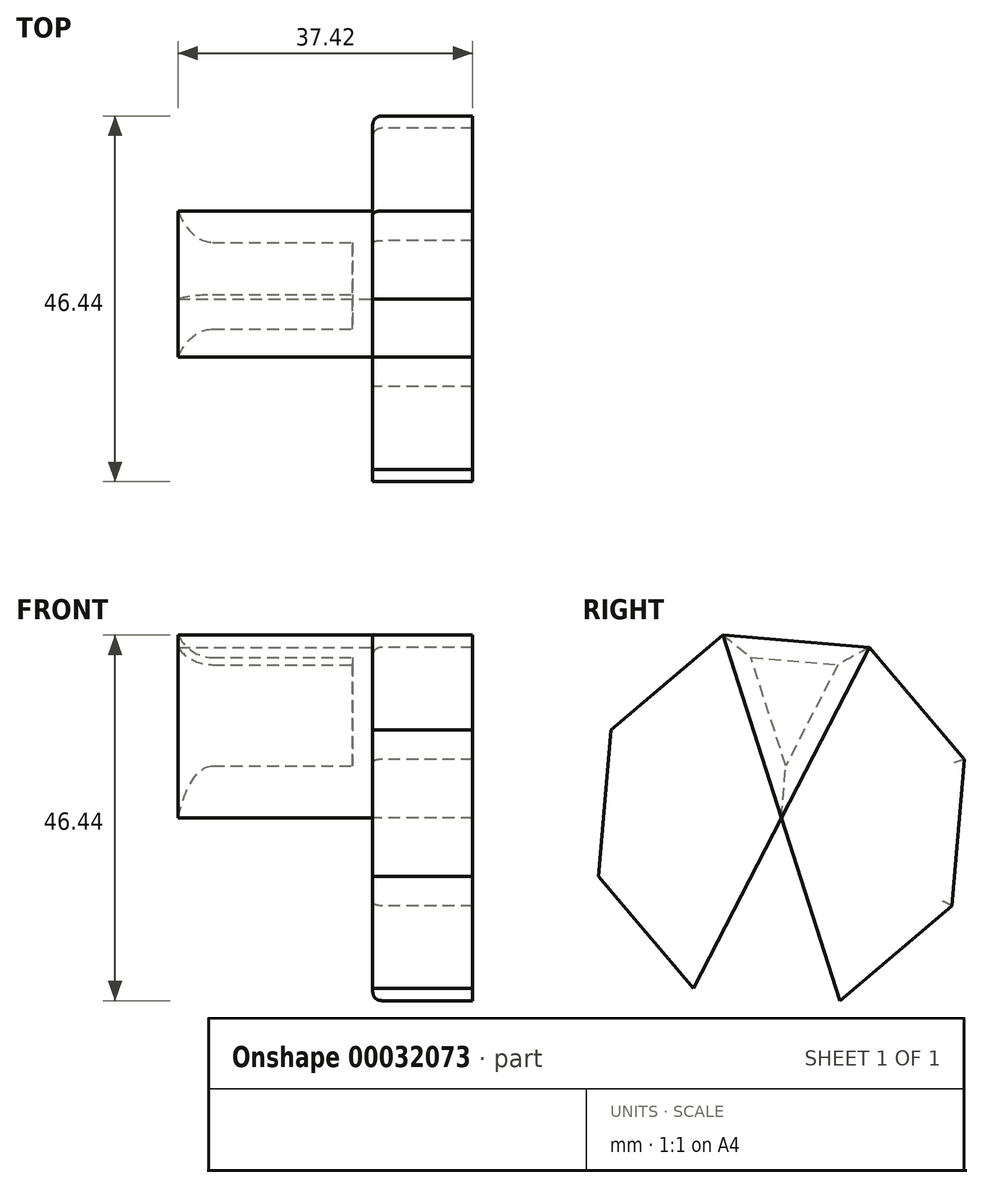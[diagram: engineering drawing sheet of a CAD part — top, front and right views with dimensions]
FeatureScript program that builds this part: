
annotation { "Feature Type Name" : "Feature", "Feature Type Description" : "" }
export const myFeature = defineFeature(function(context is Context, id is Id, definition is map)
    precondition{}
    {
        {
            var Q0;
            Q0=qCreatedBy(makeId("Right.planeOp"),FACE);
            var sketch = newSketch(context, id + "F0", { "sketchPlane" : qUnion([Q0])});
            skCircle(sketch, "E0.cCircle", {"center": v(0, 0) * mm, "radius": 24.38 * mm, "construction": true});
            skLineSegment(sketch, "E0.0", {"start": v(-21.67, 11.17) * mm, "end": v(-7.42, 23.22) * mm});
            skLineSegment(sketch, "E0.1", {"start": v(-7.42, 23.22) * mm, "end": v(11.17, 21.67) * mm});
            skLineSegment(sketch, "E0.2", {"start": v(11.17, 21.67) * mm, "end": v(23.22, 7.42) * mm});
            skLineSegment(sketch, "E0.3", {"start": v(23.22, 7.42) * mm, "end": v(21.67, -11.17) * mm});
            skLineSegment(sketch, "E0.4", {"start": v(21.67, -11.17) * mm, "end": v(7.42, -23.22) * mm});
            skLineSegment(sketch, "E0.5", {"start": v(7.42, -23.22) * mm, "end": v(-11.17, -21.67) * mm});
            skLineSegment(sketch, "E0.6", {"start": v(-11.17, -21.67) * mm, "end": v(-23.22, -7.42) * mm});
            skLineSegment(sketch, "E0.7", {"start": v(-23.22, -7.42) * mm, "end": v(-21.67, 11.17) * mm});
            skLineSegment(sketch, "E1", {"start": v(0, 0) * mm, "end": v(-7.42, 23.22) * mm});
            skLineSegment(sketch, "E2", {"start": v(11.17, 21.67) * mm, "end": v(0, 0) * mm});
            skLineSegment(sketch, "E3", {"start": v(-11.17, -21.67) * mm, "end": v(0, 0) * mm});
            skLineSegment(sketch, "E4", {"start": v(7.42, -23.22) * mm, "end": v(0, 0) * mm});
            skSolve(sketch);
        }
        {
            var Q0;
            Q0=makeQuery(id+"F0.imprint","IMPRINT",FACE,{"disambiguationData":[TD([[makeQuery(id+"F0.imprint","IMPRINT",EDGE,{"derivedFrom":sQuery(id+"F0.wireOp",EDGE,"E0.0")}),-1.0]])]});
            var Q1;
            Q1=makeQuery(id+"F0.imprint","IMPRINT",FACE,{"disambiguationData":[TD([[makeQuery(id+"F0.imprint","IMPRINT",EDGE,{"derivedFrom":sQuery(id+"F0.wireOp",EDGE,"E0.2")}),-1.0]])]});
            extrude(context, id + "F1", {"entities" : qUnion([Q0, Q1]), "depth" : 12.7 * mm});
        }
        {
            var Q0;
            Q0=makeQuery(id+"F0.imprint","IMPRINT",FACE,{"disambiguationData":[TD([[makeQuery(id+"F0.imprint","IMPRINT",EDGE,{"derivedFrom":sQuery(id+"F0.wireOp",EDGE,"E0.1")}),-1.0]])]});
            extrude(context, id + "F2", {"entities" : qUnion([Q0]), "oppositeDirection" : true, "depth" : 25.4 * mm});
        }
        {
            var Q0;
            Q0=makeQuery(id+"F1.opExtrude","CAP_EDGE",EDGE,{"disambiguationData":[OSD([sQuery(id+"F0.wireOp",EDGE,"E0.4")])],"isStart":true});
            var Q1;
            Q1=makeQuery(id+"F1.opExtrude","CAP_EDGE",EDGE,{"disambiguationData":[OSD([sQuery(id+"F0.wireOp",EDGE,"E0.3")])],"isStart":true});
            var Q2;
            Q2=makeQuery(id+"F1.opExtrude","CAP_EDGE",EDGE,{"disambiguationData":[OSD([sQuery(id+"F0.wireOp",EDGE,"E0.2")])],"isStart":true});
            fillet(context, id + "F3", {"entities" : qUnion([Q0, Q1, Q2]), "radius" : 1.27 * mm, "tangentPropagation" : true, "rho" : 0.5, "crossSection" : FilletCrossSection.CONIC, "allowEdgeOverflow" : false});
        }
        {
            var Q0;
            Q0=makeQuery(id+"F2.opExtrude","CAP_FACE",FACE,{"disambiguationData":[OSD([sQuery(id+"F0.wireOp",EDGE,"E0.1"),sQuery(id+"F0.wireOp",EDGE,"E1"),sQuery(id+"F0.wireOp",EDGE,"E2")])],"isStart":false});
            shell(context, id + "F4", {"entities" : qUnion([Q0]), "thickness" : 2.54 * mm});
        }
        {
            var Q0;
            {var subQ0=sQuery(id+"F0.wireOp",EDGE,"E0.1");Q0=makeQuery(id+"F4.opShell","OFFSET_EDGE",EDGE,{"disambiguationData":[OSD([subQ0]),TDD([makeQuery(id+"F2.opExtrude","CAP_EDGE",EDGE,{"disambiguationData":[OSD([subQ0])],"isStart":false})])]});}
            var Q1;
            {var subQ0=sQuery(id+"F0.wireOp",EDGE,"E2");Q1=makeQuery(id+"F4.opShell","OFFSET_EDGE",EDGE,{"disambiguationData":[OSD([subQ0]),TDD([makeQuery(id+"F2.opExtrude","CAP_EDGE",EDGE,{"disambiguationData":[OSD([subQ0])],"isStart":false})])]});}
            var Q2;
            {var subQ0=sQuery(id+"F0.wireOp",EDGE,"E1");Q2=makeQuery(id+"F4.opShell","OFFSET_EDGE",EDGE,{"disambiguationData":[OSD([subQ0]),TDD([makeQuery(id+"F2.opExtrude","CAP_EDGE",EDGE,{"disambiguationData":[OSD([subQ0])],"isStart":false})])]});}
            fillet(context, id + "F5", {"entities" : qUnion([Q0, Q1, Q2]), "radius" : 5.08 * mm, "tangentPropagation" : true, "allowEdgeOverflow" : false});
        }
    });
